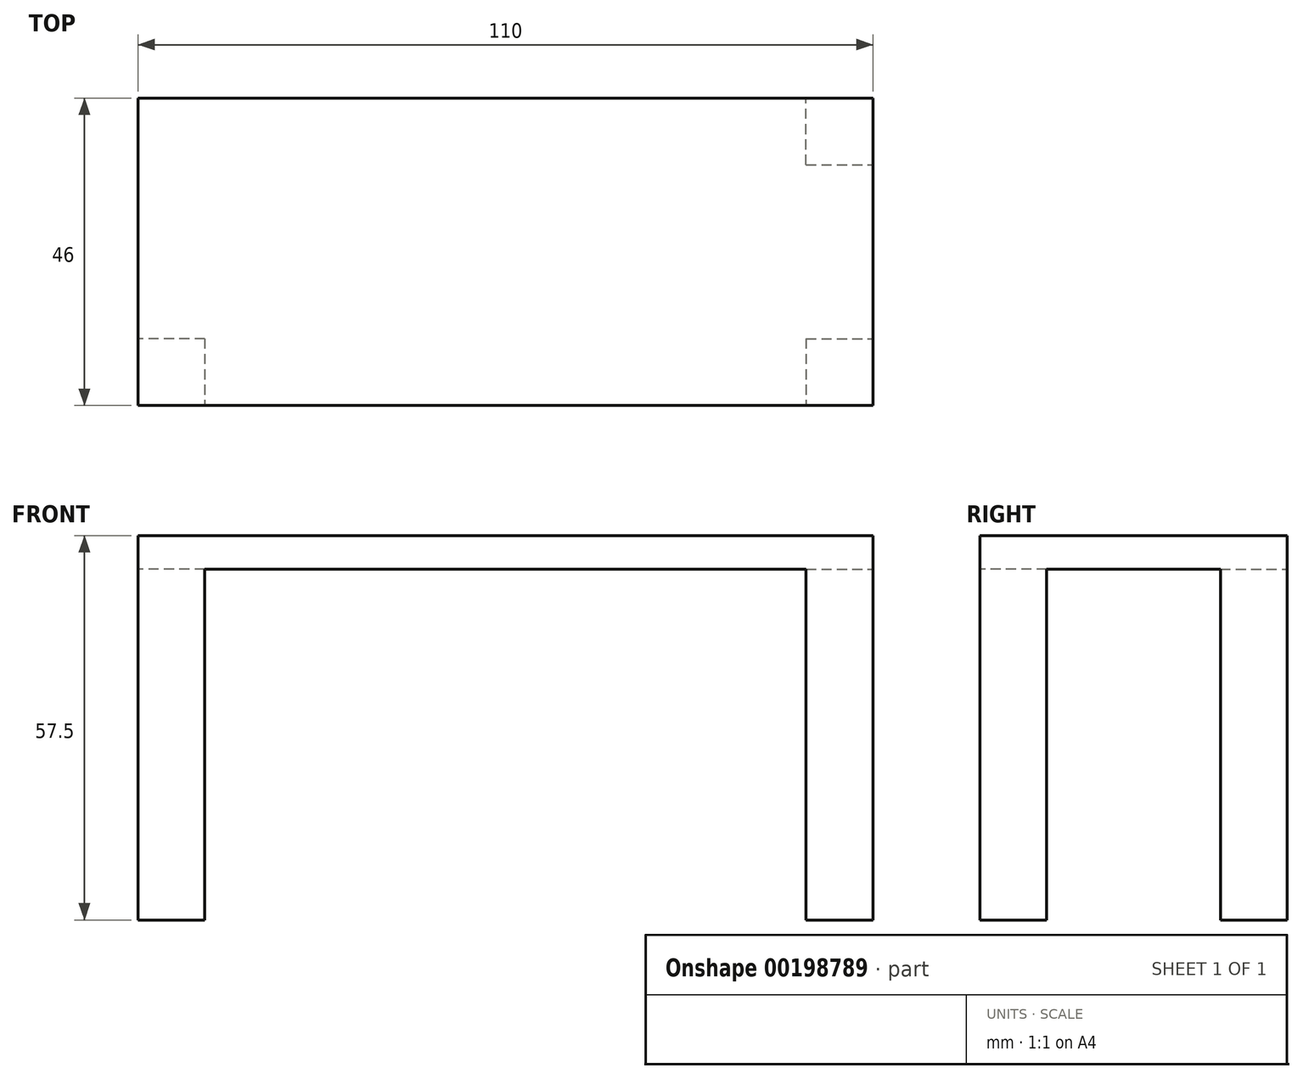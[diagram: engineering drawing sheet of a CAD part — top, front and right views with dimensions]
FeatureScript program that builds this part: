
annotation { "Feature Type Name" : "Feature", "Feature Type Description" : "" }
export const myFeature = defineFeature(function(context is Context, id is Id, definition is map)
    precondition{}
    {
        {
            var Q0;
            Q0=qCreatedBy(makeId("Top.planeOp"),FACE);
            var sketch = newSketch(context, id + "F0", { "sketchPlane" : qUnion([Q0])});
            skLineSegment(sketch, "E0.bottom", {"start": v(-45, 13) * mm, "end": v(45, 13) * mm});
            skLineSegment(sketch, "E0.top", {"start": v(-45, -13) * mm, "end": v(45, -13) * mm});
            skLineSegment(sketch, "E0.left", {"start": v(-45, 13) * mm, "end": v(-45, -13) * mm});
            skLineSegment(sketch, "E0.right", {"start": v(45, 13) * mm, "end": v(45, -13) * mm});
            skPoint(sketch, "E0.middle", {"position": v(0, 0) * mm});
            skLineSegment(sketch, "E1.bottom", {"start": v(-55, 23) * mm, "end": v(55, 23) * mm});
            skLineSegment(sketch, "E1.top", {"start": v(-55, -23) * mm, "end": v(55, -23) * mm});
            skLineSegment(sketch, "E1.left", {"start": v(-55, 23) * mm, "end": v(-55, -23) * mm});
            skLineSegment(sketch, "E1.right", {"start": v(55, 23) * mm, "end": v(55, -23) * mm});
            skLineSegment(sketch, "E2.bottom", {"start": v(-55, 23) * mm, "end": v(-45, 23) * mm});
            skLineSegment(sketch, "E2.top", {"start": v(-55, 13) * mm, "end": v(-45, 13) * mm});
            skLineSegment(sketch, "E2.left", {"start": v(-55, 23) * mm, "end": v(-55, 13) * mm});
            skLineSegment(sketch, "E2.right", {"start": v(-45, 23) * mm, "end": v(-45, 13) * mm});
            skLineSegment(sketch, "E3.bottom", {"start": v(45, 13) * mm, "end": v(55, 13) * mm});
            skLineSegment(sketch, "E3.top", {"start": v(45, 23) * mm, "end": v(55, 23) * mm});
            skLineSegment(sketch, "E3.left", {"start": v(45, 13) * mm, "end": v(45, 23) * mm});
            skLineSegment(sketch, "E3.right", {"start": v(55, 13) * mm, "end": v(55, 23) * mm});
            skLineSegment(sketch, "E4.bottom", {"start": v(45, -13) * mm, "end": v(55, -13) * mm});
            skLineSegment(sketch, "E4.top", {"start": v(45, -23) * mm, "end": v(55, -23) * mm});
            skLineSegment(sketch, "E4.left", {"start": v(45, -13) * mm, "end": v(45, -23) * mm});
            skLineSegment(sketch, "E4.right", {"start": v(55, -13) * mm, "end": v(55, -23) * mm});
            skLineSegment(sketch, "E5.bottom", {"start": v(-45, -13) * mm, "end": v(-55, -13) * mm});
            skLineSegment(sketch, "E5.top", {"start": v(-45, -23) * mm, "end": v(-55, -23) * mm});
            skLineSegment(sketch, "E5.left", {"start": v(-45, -13) * mm, "end": v(-45, -23) * mm});
            skLineSegment(sketch, "E5.right", {"start": v(-55, -13) * mm, "end": v(-55, -23) * mm});
            skSolve(sketch);
        }
        {
            var Q0;
            Q0 = qSketchRegion(id + "F0", true);
            extrude(context, id + "F1", {"entities" : qUnion([Q0]), "oppositeDirection" : true, "depth" : 5 * mm});
        }
        {
            var Q0;
            Q0=makeQuery(id+"F0.imprint","IMPRINT",FACE,{"disambiguationData":[TD([[makeQuery(id+"F0.imprint","IMPRINT",EDGE,{"derivedFrom":sQuery(id+"F0.wireOp",EDGE,"E0.bottom")}),-1.0]])]});
            extrude(context, id + "F2", {"entities" : qUnion([Q0]), "operationType" : NewBodyOperationType.ADD, "oppositeDirection" : true, "depth" : 5 * mm});
        }
        {
            var Q0;
            Q0=makeQuery(id+"F0.imprint","IMPRINT",FACE,{"disambiguationData":[TD([[makeQuery(id+"F0.imprint","IMPRINT",EDGE,{"derivedFrom":sQuery(id+"F0.wireOp",EDGE,"E2.bottom")}),-1.0]])]});
            var Q1;
            Q1=makeQuery(id+"F0.imprint","IMPRINT",FACE,{"disambiguationData":[TD([[makeQuery(id+"F0.imprint","IMPRINT",EDGE,{"derivedFrom":sQuery(id+"F0.wireOp",EDGE,"E3.bottom")}),1.0]])]});
            var Q2;
            Q2=makeQuery(id+"F0.imprint","IMPRINT",FACE,{"disambiguationData":[TD([[makeQuery(id+"F0.imprint","IMPRINT",EDGE,{"derivedFrom":sQuery(id+"F0.wireOp",EDGE,"E4.bottom")}),-1.0]])]});
            var Q3;
            Q3=makeQuery(id+"F0.imprint","IMPRINT",FACE,{"disambiguationData":[TD([[makeQuery(id+"F0.imprint","IMPRINT",EDGE,{"derivedFrom":sQuery(id+"F0.wireOp",EDGE,"E5.bottom")}),1.0]])]});
            extrude(context, id + "F3", {"entities" : qUnion([Q0, Q1, Q2, Q3]), "operationType" : NewBodyOperationType.ADD, "oppositeDirection" : true, "depth" : 57.5 * mm});
        }
    });
